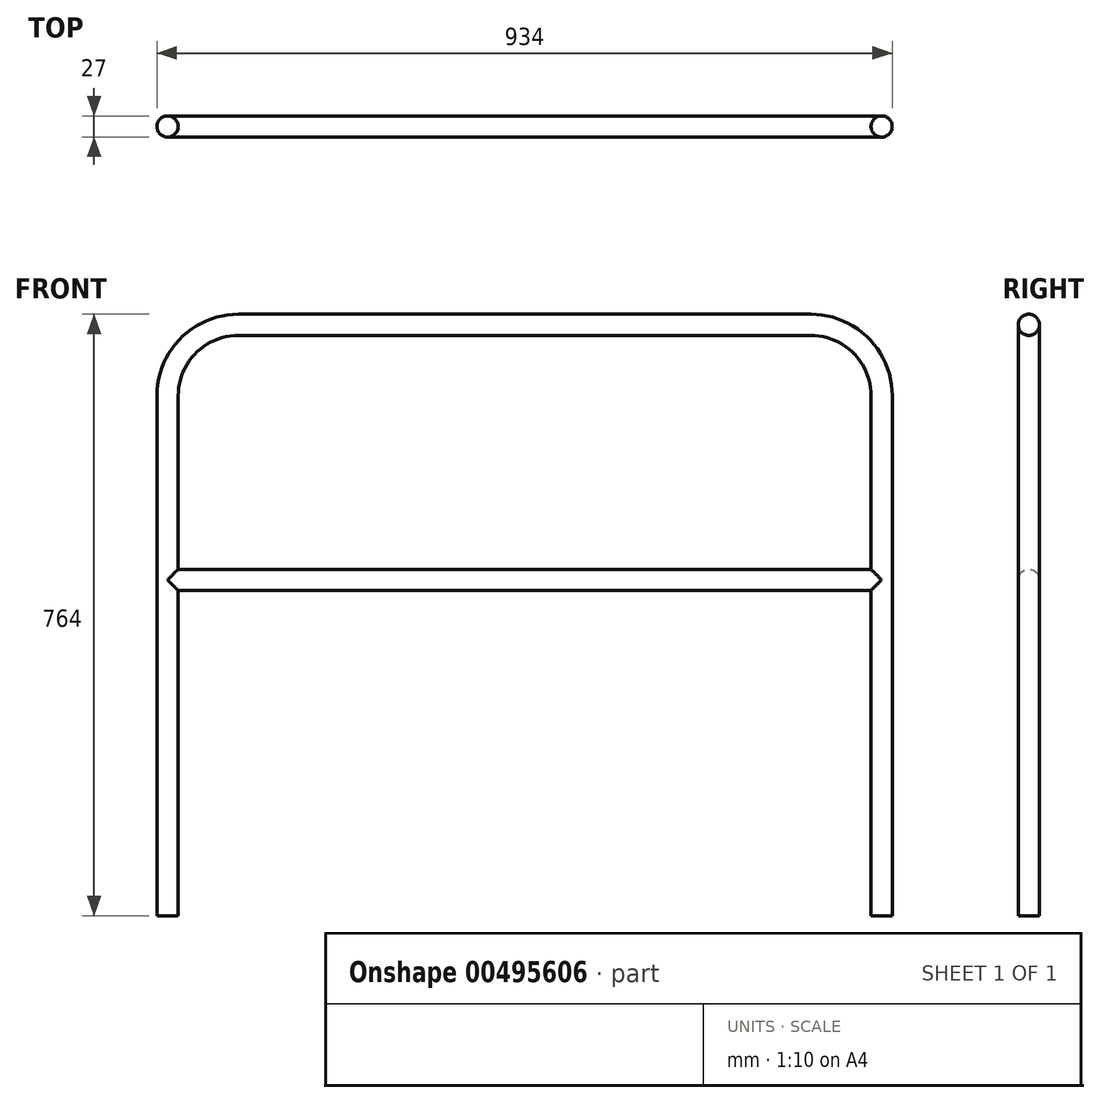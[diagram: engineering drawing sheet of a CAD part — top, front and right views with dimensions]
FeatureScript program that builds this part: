
annotation { "Feature Type Name" : "Feature", "Feature Type Description" : "" }
export const myFeature = defineFeature(function(context is Context, id is Id, definition is map)
    precondition{}
    {
        {
            var Q0;
            Q0=qCreatedBy(makeId("Front.planeOp"),FACE);
            var sketch = newSketch(context, id + "F0", { "sketchPlane" : qUnion([Q0])});
            skLineSegment(sketch, "E0", {"start": v(-453.5, -750.5) * mm, "end": v(-453.5, -90) * mm});
            skLineSegment(sketch, "E1", {"start": v(-363.5, 0) * mm, "end": v(363.5, 0) * mm});
            skLineSegment(sketch, "E2", {"start": v(453.5, -90) * mm, "end": v(453.5, -750.5) * mm});
            skPoint(sketch, "E3.visualSharp", {"position": v(-453.5, 0) * mm});
            skArc(sketch, "E3.filletArc", {"start": v(-363.5, 0) * mm, "mid": v(-427.14, -26.36) * mm, "end": v(-453.5, -90) * mm});
            skPoint(sketch, "E4.visualSharp", {"position": v(453.5, 0) * mm});
            skArc(sketch, "E4.filletArc", {"start": v(453.5, -90) * mm, "mid": v(427.14, -26.36) * mm, "end": v(363.5, 0) * mm});
            skSolve(sketch);
        }
        {
            var Q0;
            Q0=sQuery(id+"F0.wireOp",VERTEX,"E2.end");
            var Q1;
            Q1=qCreatedBy(makeId("Top.planeOp"),FACE);
            cPlane(context, id + "F1", {"entities" : qUnion([Q0, Q1]), "cplaneType" : CPlaneType.PLANE_POINT, "offset" : 25.4 * mm, "width" : 152.4 * mm, "height" : 152.4 * mm});
        }
        {
            var Q0;
            Q0=qCreatedBy(id+"F1.planeOp",FACE);
            var sketch = newSketch(context, id + "F2", { "sketchPlane" : qUnion([Q0])});
            skCircle(sketch, "E5", {"center": v(453.5, 0) * mm, "radius": 13.5 * mm});
            skSolve(sketch);
        }
        {
            var Q0;
            Q0=makeQuery(id+"F2.imprint","IMPRINT",FACE,{"disambiguationData":[TD([[makeQuery(id+"F2.imprint","IMPRINT",EDGE,{"derivedFrom":sQuery(id+"F2.wireOp",EDGE,"E5")}),1.0]])]});
            var Q1;
            Q1=sQuery(id+"F0.wireOp",EDGE,"E2");
            var Q2;
            Q2=sQuery(id+"F0.wireOp",EDGE,"E4.filletArc");
            var Q3;
            Q3=sQuery(id+"F0.wireOp",EDGE,"E1");
            var Q4;
            Q4=sQuery(id+"F0.wireOp",EDGE,"E3.filletArc");
            var Q5;
            Q5=sQuery(id+"F0.wireOp",EDGE,"E0");
            sweep(context, id + "F3", {"profiles" : qUnion([Q0]), "path" : qUnion([Q1, Q2, Q3, Q4, Q5])});
        }
        {
            var Q0;
            Q0=qCreatedBy(makeId("Right.planeOp"),FACE);
            var sketch = newSketch(context, id + "F4", { "sketchPlane" : qUnion([Q0])});
            skCircle(sketch, "E6", {"center": v(0, -324) * mm, "radius": 13.5 * mm});
            skSolve(sketch);
        }
        {
            var Q0;
            Q0 = qSketchRegion(id + "F4", true);
            var Q1;
            Q1=makeQuery(id+"F3.opSweep","SWEPT_BODY",BODY,{"disambiguationData":[OSD([sQuery(id+"F0.wireOp",EDGE,"E0"),sQuery(id+"F2.wireOp",EDGE,"E5")])]});
            var Q2;
            Q2=makeQuery(id+"F3.opSweep","SWEPT_BODY",BODY,{"disambiguationData":[OSD([sQuery(id+"F0.wireOp",EDGE,"E0"),sQuery(id+"F2.wireOp",EDGE,"E5")])]});
            extrude(context, id + "F5", {"entities" : qUnion([Q0]), "operationType" : NewBodyOperationType.ADD, "endBound" : BoundingType.UP_TO_BODY, "endBoundEntityBody" : qUnion([Q1]), "depth" : 25.4 * mm, "hasSecondDirection" : true, "secondDirectionBound" : SecondDirectionBoundingType.UP_TO_BODY, "secondDirectionOppositeDirection" : true, "secondDirectionBoundEntityBody" : qUnion([Q2]), "secondDirectionDepth" : 25.4 * mm});
        }
    });
